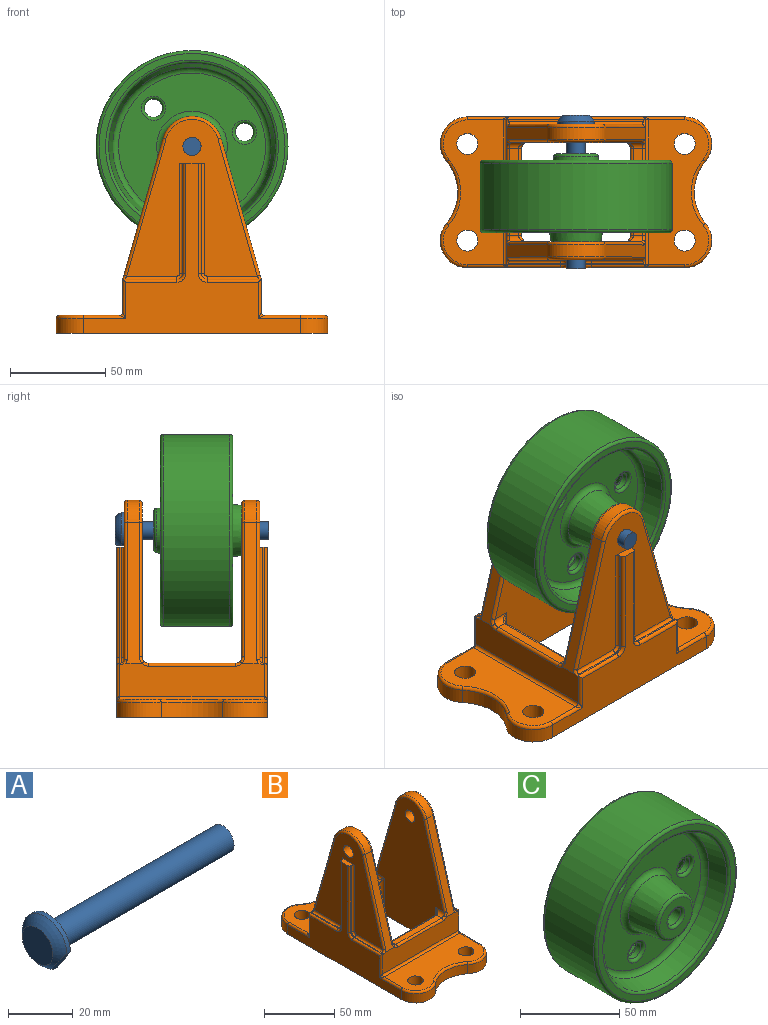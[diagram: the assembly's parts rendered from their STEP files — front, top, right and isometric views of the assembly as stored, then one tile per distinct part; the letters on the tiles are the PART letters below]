
ASSEMBLY  parts=3 mates=2
PART A: 7 faces, bbox 81x19.1x19.1 mm
  f0: sphere r=11.11mm, area 202.5mm2, adj f2,f3,f6
  f1: plane 19.05x19.05mm, normal (1,0,0), area 202.4mm2, adj f3,f4,f6
  f2: plane 13.31x13.31mm, normal (-1,0,0), area 139.2mm2, adj f0
  f3: cylinder r=9.53mm len=19.05mm, axis (-1,0,0), area 77.3mm2, adj f0,f1,f6
  f4: cylinder r=4.76mm len=76.2mm, axis (-1,0,0), area 2280.2mm2, adj f1,f5
  f5: plane 9.53x9.53mm, normal (1,0,0), area 71.3mm2, adj f4
  f6: plane 8.78x5.82mm, normal (0,-0.83,-0.55), area 31.6mm2, adj f0,f1,f3
PART B: 131 faces, bbox 81.8x145.3x115.7 mm
  f0: plane 114.3x89.69mm, normal (-1,0,0), area 2645.8mm2, adj f8,f11,f13,f35,f36,f37,f38,f39
  f1: cylinder r=25.4mm len=32.51mm, axis (0,0,-1), area 280mm2, adj f11,f13,f33,f81
  f2: plane 76.2x31.75mm, normal (0,0,1), area 1891.8mm2, adj f12,f33,f34,f35,f40,f82,f100,f101
  f3: plane 112.71x67.9mm, normal (1,0,0), area 5118.5mm2, adj f10,f13,f18,f19,f26,f27,f53,f54
  f4: plane 46.04x26.99mm, normal (0,1,0), area 1242.4mm2, adj f13,f19,f29,f88
  f5: plane 76.2x17.46mm, normal (0,-1,0), area 1247.4mm2, adj f14,f25,f31,f32,f36,f40,f83,f94
  f6: plane 46.04x4.76mm, normal (0,0,1), area 219.3mm2, adj f18,f29,f31,f87
  f7: cylinder r=15.88mm len=30.52mm, axis (-1,0,0), area 260.5mm2, adj f14,f23,f26,f49
  f8: plane 12.7x3.97mm, normal (0,0,1), area 37.8mm2, adj f0,f9,f15,f20,f39,f50,f55,f72
  f9: plane 82.55x68.81mm, normal (-1,0,0), area 2857mm2, adj f8,f10,f20,f21,f22,f23,f24,f55
  f10: cylinder r=4.76mm len=9.53mm, axis (-1,0,0), area 285mm2, adj f3,f9
  f11: cylinder r=14.29mm len=23.43mm, axis (0,0,-1), area 256.9mm2, adj f0,f1,f13,f34
  f12: cylinder r=5.56mm len=11.11mm, axis (0,0,-1), area 332.5mm2, adj f2,f13
  f13: plane 142.88x79.38mm, normal (0,0,-1), area 7277.2mm2, adj f0,f1,f3,f4,f11,f12,f19,f42
  f14: plane 74.22x21.25mm, normal (0,-0.96,0.28), area 492.6mm2, adj f5,f7,f24,f25,f27,f28,f32
  f15: plane 57.94x0.79mm, normal (0,-1,0), area 46mm2, adj f8,f17,f20,f39
  f16: plane 28.09x0.84mm, normal (0,0,1), area 22mm2, adj f17,f22,f25,f37
  f17: cylinder r=3.17mm len=3.18mm, axis (1,0,0), area 4mm2, adj f15,f16,f21,f38
  f18: cylinder r=3.17mm len=9.53mm, axis (0,-1,0), area 34.4mm2, adj f3,f6,f28,f30,f32
  f19: cylinder r=3.17mm len=31.75mm, axis (0,0,-1), area 146.5mm2, adj f3,f4,f13,f30
  f20: cylinder r=1.59mm len=57.94mm, axis (0,0,-1), area 144.5mm2, adj f8,f9,f15,f21
  f21: torus R=1.59mm, axis (-1,0,0), area 10.2mm2, adj f9,f17,f20,f22
  f22: cylinder r=1.59mm len=27.38mm, axis (0,-1,0), area 67.1mm2, adj f9,f16,f21,f25
  f23: torus R=14.29mm, axis (-1,0,0), area 98.6mm2, adj f7,f9,f24,f58
  f24: cylinder r=1.59mm len=72.63mm, axis (0,0.28,0.96), area 187.3mm2, adj f9,f14,f23,f25
  f25: bspline ~4.96x3.17mm, area 7.7mm2, adj f5,f14,f16,f22,f24,f36,f37
  f26: torus R=14.29mm, axis (1,0,0), area 98.6mm2, adj f3,f7,f27,f60
  f27: cylinder r=1.59mm len=71.04mm, axis (0,0.28,0.96), area 183.1mm2, adj f3,f14,f26,f28
  f28: bspline ~4.11x2.94mm, area 7.6mm2, adj f14,f18,f27,f32
  f29: cylinder r=1.59mm len=46.04mm, axis (1,0,0), area 114.8mm2, adj f4,f6,f30,f98
  f30: bspline ~4.76x4.76mm, area 5.4mm2, adj f18,f19,f29
  f31: cylinder r=1.59mm len=46.04mm, axis (-1,0,0), area 114.8mm2, adj f5,f6,f32,f99
  f32: torus R=4.76mm, axis (0,1,0), area 7.5mm2, adj f5,f14,f18,f28,f31
  f33: torus R=26.99mm, axis (0,0,1), area 90mm2, adj f1,f2,f34,f100
  f34: torus R=12.7mm, axis (0,0,1), area 77.4mm2, adj f2,f11,f33,f35
  f35: cylinder r=1.59mm len=22.23mm, axis (0,1,0), area 51.5mm2, adj f0,f2,f34,f41
  f36: cylinder r=1.59mm len=20.52mm, axis (0,0,1), area 44.6mm2, adj f0,f5,f25,f37,f41
  f37: cylinder r=1.59mm len=28.46mm, axis (0,1,0), area 69.5mm2, adj f0,f16,f25,f36,f38
  f38: torus R=4.76mm, axis (-1,0,0), area 14.7mm2, adj f0,f17,f37,f39
  f39: cylinder r=1.59mm len=57.94mm, axis (0,0,1), area 144.5mm2, adj f0,f8,f15,f38
  f40: cylinder r=1.59mm len=76.2mm, axis (1,0,0), area 190mm2, adj f2,f5,f41,f106
  f41: bspline ~3.18x3.18mm, area 2.7mm2, adj f35,f36,f40
  f42: cylinder r=25.4mm len=32.51mm, axis (0,0,-1), area 280mm2, adj f13,f47,f66,f107
  f43: plane 76.2x31.75mm, normal (0,0,1), area 1891.8mm2, adj f48,f66,f67,f68,f73,f108,f124,f125
  f44: plane 46.04x26.99mm, normal (0,-1,0), area 1242.4mm2, adj f13,f54,f62,f114
  f45: plane 76.2x17.46mm, normal (0,1,0), area 1247.4mm2, adj f49,f59,f64,f65,f69,f73,f109,f119
  f46: plane 46.04x4.76mm, normal (0,0,1), area 219.3mm2, adj f53,f62,f64,f113
  f47: cylinder r=14.29mm len=23.43mm, axis (0,0,-1), area 256.9mm2, adj f0,f13,f42,f67
  f48: cylinder r=5.56mm len=11.11mm, axis (0,0,-1), area 332.5mm2, adj f13,f43
  f49: plane 74.22x21.25mm, normal (0,0.96,0.28), area 492.6mm2, adj f7,f45,f58,f59,f60,f61,f65
  f50: plane 57.94x0.79mm, normal (0,1,0), area 46mm2, adj f8,f52,f55,f72
  f51: plane 28.09x0.84mm, normal (0,0,1), area 22mm2, adj f52,f57,f59,f70
  f52: cylinder r=3.17mm len=3.18mm, axis (1,0,0), area 4mm2, adj f50,f51,f56,f71
  f53: cylinder r=3.17mm len=9.53mm, axis (0,1,0), area 34.4mm2, adj f3,f46,f61,f63,f65
  f54: cylinder r=3.17mm len=31.75mm, axis (0,0,-1), area 146.5mm2, adj f3,f13,f44,f63
  f55: cylinder r=1.59mm len=57.94mm, axis (0,0,-1), area 144.5mm2, adj f8,f9,f50,f56
  f56: torus R=1.59mm, axis (-1,0,0), area 10.2mm2, adj f9,f52,f55,f57
  f57: cylinder r=1.59mm len=27.38mm, axis (0,1,0), area 67.1mm2, adj f9,f51,f56,f59
  f58: cylinder r=1.59mm len=72.63mm, axis (0,-0.28,0.96), area 187.3mm2, adj f9,f23,f49,f59
  f59: bspline ~4.96x3.17mm, area 7.7mm2, adj f45,f49,f51,f57,f58,f69,f70
  f60: cylinder r=1.59mm len=71.04mm, axis (0,-0.28,0.96), area 183.1mm2, adj f3,f26,f49,f61
  f61: bspline ~3.51x2.61mm, area 7.6mm2, adj f49,f53,f60,f65
  f62: cylinder r=1.59mm len=46.04mm, axis (1,0,0), area 114.8mm2, adj f44,f46,f63,f122
  f63: bspline ~4.76x4.76mm, area 5.4mm2, adj f53,f54,f62
  f64: cylinder r=1.59mm len=46.04mm, axis (-1,0,0), area 114.8mm2, adj f45,f46,f65,f123
  f65: torus R=4.76mm, axis (0,-1,0), area 7.5mm2, adj f45,f49,f53,f61,f64
  f66: torus R=26.99mm, axis (0,0,1), area 90mm2, adj f42,f43,f67,f124
  f67: torus R=12.7mm, axis (0,0,1), area 77.4mm2, adj f43,f47,f66,f68
  f68: cylinder r=1.59mm len=22.23mm, axis (0,-1,0), area 51.5mm2, adj f0,f43,f67,f74
  f69: cylinder r=1.59mm len=20.52mm, axis (0,0,1), area 44.6mm2, adj f0,f45,f59,f70,f74
  f70: cylinder r=1.59mm len=28.46mm, axis (0,-1,0), area 69.5mm2, adj f0,f51,f59,f69,f71
  f71: torus R=4.76mm, axis (-1,0,0), area 14.7mm2, adj f0,f52,f70,f72
  f72: cylinder r=1.59mm len=57.94mm, axis (0,0,1), area 144.5mm2, adj f0,f8,f50,f71
  f73: cylinder r=1.59mm len=76.2mm, axis (1,0,0), area 190mm2, adj f43,f45,f74,f130
  f74: bspline ~3.18x3.18mm, area 2.7mm2, adj f68,f69,f73
  f75: plane 114.3x89.69mm, normal (1,0,0), area 2645.8mm2, adj f13,f78,f81,f101,f102,f103,f104,f105
  f76: plane 112.71x67.9mm, normal (-1,0,0), area 5118.5mm2, adj f13,f80,f87,f88,f95,f96,f113,f114
  f77: cylinder r=15.88mm len=30.52mm, axis (1,0,0), area 260.5mm2, adj f83,f92,f95,f109
  f78: plane 12.7x3.97mm, normal (0,0,1), area 37.8mm2, adj f75,f79,f84,f89,f105,f110,f115,f129
  f79: plane 82.55x68.81mm, normal (1,0,0), area 2857mm2, adj f78,f80,f89,f90,f91,f92,f93,f115
  f80: cylinder r=4.76mm len=9.53mm, axis (1,0,0), area 285mm2, adj f76,f79
  f81: cylinder r=14.29mm len=23.43mm, axis (0,0,-1), area 256.9mm2, adj f1,f13,f75,f100
  f82: cylinder r=5.56mm len=11.11mm, axis (0,0,-1), area 332.5mm2, adj f2,f13
  f83: plane 74.22x21.25mm, normal (0,-0.96,0.28), area 492.6mm2, adj f5,f77,f93,f94,f96,f97,f99
  f84: plane 57.94x0.79mm, normal (0,-1,0), area 46mm2, adj f78,f86,f89,f105
  f85: plane 28.09x0.84mm, normal (0,0,1), area 22mm2, adj f86,f91,f94,f103
  f86: cylinder r=3.17mm len=3.18mm, axis (-1,0,0), area 4mm2, adj f84,f85,f90,f104
  f87: cylinder r=3.17mm len=9.53mm, axis (0,-1,0), area 34.4mm2, adj f6,f76,f97,f98,f99
  f88: cylinder r=3.17mm len=31.75mm, axis (0,0,-1), area 146.5mm2, adj f4,f13,f76,f98
  f89: cylinder r=1.59mm len=57.94mm, axis (0,0,-1), area 144.5mm2, adj f78,f79,f84,f90
  f90: torus R=1.59mm, axis (1,0,0), area 10.2mm2, adj f79,f86,f89,f91
  f91: cylinder r=1.59mm len=27.38mm, axis (0,-1,0), area 67.1mm2, adj f79,f85,f90,f94
  f92: torus R=14.29mm, axis (1,0,0), area 98.6mm2, adj f77,f79,f93,f118
  f93: cylinder r=1.59mm len=72.63mm, axis (0,0.28,0.96), area 187.3mm2, adj f79,f83,f92,f94
  f94: bspline ~4.96x3.17mm, area 7.7mm2, adj f5,f83,f85,f91,f93,f102,f103
  f95: torus R=14.29mm, axis (-1,0,0), area 98.6mm2, adj f76,f77,f96,f120
  f96: cylinder r=1.59mm len=71.04mm, axis (0,0.28,0.96), area 183.1mm2, adj f76,f83,f95,f97
  f97: bspline ~4.11x2.94mm, area 7.6mm2, adj f83,f87,f96,f99
  f98: bspline ~4.76x4.76mm, area 5.4mm2, adj f29,f87,f88
  f99: torus R=4.76mm, axis (0,1,0), area 7.5mm2, adj f5,f31,f83,f87,f97
  f100: torus R=12.7mm, axis (0,0,1), area 77.4mm2, adj f2,f33,f81,f101
  f101: cylinder r=1.59mm len=22.23mm, axis (0,1,0), area 51.5mm2, adj f2,f75,f100,f106
  f102: cylinder r=1.59mm len=20.52mm, axis (0,0,1), area 44.6mm2, adj f5,f75,f94,f103,f106
  f103: cylinder r=1.59mm len=28.46mm, axis (0,1,0), area 69.5mm2, adj f75,f85,f94,f102,f104
  f104: torus R=4.76mm, axis (1,0,0), area 14.7mm2, adj f75,f86,f103,f105
  f105: cylinder r=1.59mm len=57.94mm, axis (0,0,1), area 144.5mm2, adj f75,f78,f84,f104
  f106: bspline ~3.18x3.18mm, area 2.7mm2, adj f40,f101,f102
  f107: cylinder r=14.29mm len=23.43mm, axis (0,0,-1), area 256.9mm2, adj f13,f42,f75,f124
  f108: cylinder r=5.56mm len=11.11mm, axis (0,0,-1), area 332.5mm2, adj f13,f43
  f109: plane 74.22x21.25mm, normal (0,0.96,0.28), area 492.6mm2, adj f45,f77,f118,f119,f120,f121,f123
  f110: plane 57.94x0.79mm, normal (0,1,0), area 46mm2, adj f78,f112,f115,f129
  f111: plane 28.09x0.84mm, normal (0,0,1), area 22mm2, adj f112,f117,f119,f127
  f112: cylinder r=3.17mm len=3.18mm, axis (-1,0,0), area 4mm2, adj f110,f111,f116,f128
  f113: cylinder r=3.17mm len=9.53mm, axis (0,1,0), area 34.4mm2, adj f46,f76,f121,f122,f123
  f114: cylinder r=3.17mm len=31.75mm, axis (0,0,-1), area 146.5mm2, adj f13,f44,f76,f122
  f115: cylinder r=1.59mm len=57.94mm, axis (0,0,-1), area 144.5mm2, adj f78,f79,f110,f116
  f116: torus R=1.59mm, axis (1,0,0), area 10.2mm2, adj f79,f112,f115,f117
  f117: cylinder r=1.59mm len=27.38mm, axis (0,1,0), area 67.1mm2, adj f79,f111,f116,f119
  f118: cylinder r=1.59mm len=72.63mm, axis (0,-0.28,0.96), area 187.3mm2, adj f79,f92,f109,f119
  f119: bspline ~4.96x3.17mm, area 7.7mm2, adj f45,f109,f111,f117,f118,f126,f127
  f120: cylinder r=1.59mm len=71.04mm, axis (0,-0.28,0.96), area 183.1mm2, adj f76,f95,f109,f121
  f121: bspline ~3.51x2.61mm, area 7.6mm2, adj f109,f113,f120,f123
  f122: bspline ~4.76x4.76mm, area 5.4mm2, adj f62,f113,f114
  f123: torus R=4.76mm, axis (0,-1,0), area 7.5mm2, adj f45,f64,f109,f113,f121
  f124: torus R=12.7mm, axis (0,0,1), area 77.4mm2, adj f43,f66,f107,f125
  f125: cylinder r=1.59mm len=22.23mm, axis (0,-1,0), area 51.5mm2, adj f43,f75,f124,f130
  f126: cylinder r=1.59mm len=20.52mm, axis (0,0,1), area 44.6mm2, adj f45,f75,f119,f127,f130
  f127: cylinder r=1.59mm len=28.46mm, axis (0,-1,0), area 69.5mm2, adj f75,f111,f119,f126,f128
  f128: torus R=4.76mm, axis (1,0,0), area 14.7mm2, adj f75,f112,f127,f129
  f129: cylinder r=1.59mm len=57.94mm, axis (0,0,1), area 144.5mm2, adj f75,f78,f110,f128
  f130: bspline ~3.18x3.18mm, area 2.7mm2, adj f73,f125,f126
PART C: 33 faces, bbox 109.4x48.1x109.4 mm
  f0: torus R=48.95mm, axis (0,-1,0), area 782.8mm2, adj f1,f23
  f1: cylinder r=50.54mm len=101.08mm, axis (0,-1,0), area 11090.7mm2, adj f0,f2
  f2: torus R=48.95mm, axis (0,-1,0), area 782.8mm2, adj f1,f3
  f3: plane 97.91x97.91mm, normal (0,1,0), area 1025.6mm2, adj f2,f4
  f4: torus R=45.5mm, axis (0,-1,0), area 612.1mm2, adj f3,f5
  f5: cone r=41.27mm half-angle=11.1deg, axis (0,1,0), area 3711.4mm2, adj f4,f6
  f6: torus R=38.15mm, axis (0,-1,0), area 1099.3mm2, adj f5,f7
  f7: plane 76.31x76.31mm, normal (0,1,0), area 3258.3mm2, adj f6,f8,f27,f28,f29
  f8: torus R=17.25mm, axis (0,-1,0), area 437.4mm2, adj f7,f9
  f9: cone r=14.11mm half-angle=8.1deg, axis (0,-1,0), area 1374.4mm2, adj f8,f10
  f10: torus R=10.14mm, axis (0,-1,0), area 158.1mm2, adj f9,f11
  f11: plane 20.28x20.28mm, normal (0,1,0), area 193.9mm2, adj f10,f12
  f12: torus R=6.41mm, axis (0,-1,0), area 84.7mm2, adj f11,f13
  f13: cylinder r=4.83mm len=44.9mm, axis (0,-1,0), area 1361.5mm2, adj f12,f14
  f14: torus R=6.41mm, axis (0,-1,0), area 84.7mm2, adj f13,f15
  f15: plane 23.04x23.04mm, normal (0,-1,0), area 287.5mm2, adj f14,f16
  f16: torus R=11.52mm, axis (0,-1,0), area 177.8mm2, adj f15,f17
  f17: cone r=13.09mm half-angle=8.1deg, axis (0,1,0), area 1521mm2, adj f16,f18
  f18: torus R=18.63mm, axis (0,-1,0), area 476.6mm2, adj f17,f19
  f19: plane 77.36x77.36mm, normal (0,-1,0), area 3230.5mm2, adj f18,f20,f30,f31,f32
  f20: torus R=38.68mm, axis (0,-1,0), area 1107.6mm2, adj f19,f21
  f21: cone r=41.79mm half-angle=11.5deg, axis (0,-1,0), area 2882.8mm2, adj f20,f22
  f22: torus R=45.49mm, axis (0,-1,0), area 608.8mm2, adj f21,f23
  f23: plane 97.91x97.91mm, normal (0,-1,0), area 1028.4mm2, adj f0,f22
  f24: cylinder r=4.76mm len=9.53mm, axis (0,-1,0), area 95mm2, adj f29,f30
  f25: cylinder r=4.76mm len=9.53mm, axis (0,-1,0), area 95mm2, adj f28,f31
  f26: cylinder r=4.76mm len=9.53mm, axis (0,-1,0), area 95mm2, adj f27,f32
  f27: torus R=6.35mm, axis (0,-1,0), area 83.7mm2, adj f7,f26
  f28: torus R=6.35mm, axis (0,-1,0), area 83.7mm2, adj f7,f25
  f29: torus R=6.35mm, axis (0,-1,0), area 83.7mm2, adj f7,f24
  f30: torus R=6.35mm, axis (0,-1,0), area 83.7mm2, adj f19,f24
  f31: torus R=6.35mm, axis (0,-1,0), area 83.7mm2, adj f19,f25
  f32: torus R=6.35mm, axis (0,-1,0), area 83.7mm2, adj f19,f26
PLACE A rot(axis=(0.43,-0.43,-0.79),103.4deg) t=(-106.3,-29.14,-16.91)mm
PLACE B rot(axis=(0,0,-1),90deg) t=(-97.79,-46.68,-115.34)mm
PLACE C t=(-101.47,-63.64,-16.91)mm
MATE cylindrical A.f3 <-> B.f95  axis (0,-1,0) through (-106.3,-25.01,-16.91)mm
MATE revolute A.f3 <-> C.f2  axis (0,1,0) through (-106.3,-63.11,-16.91)mm
